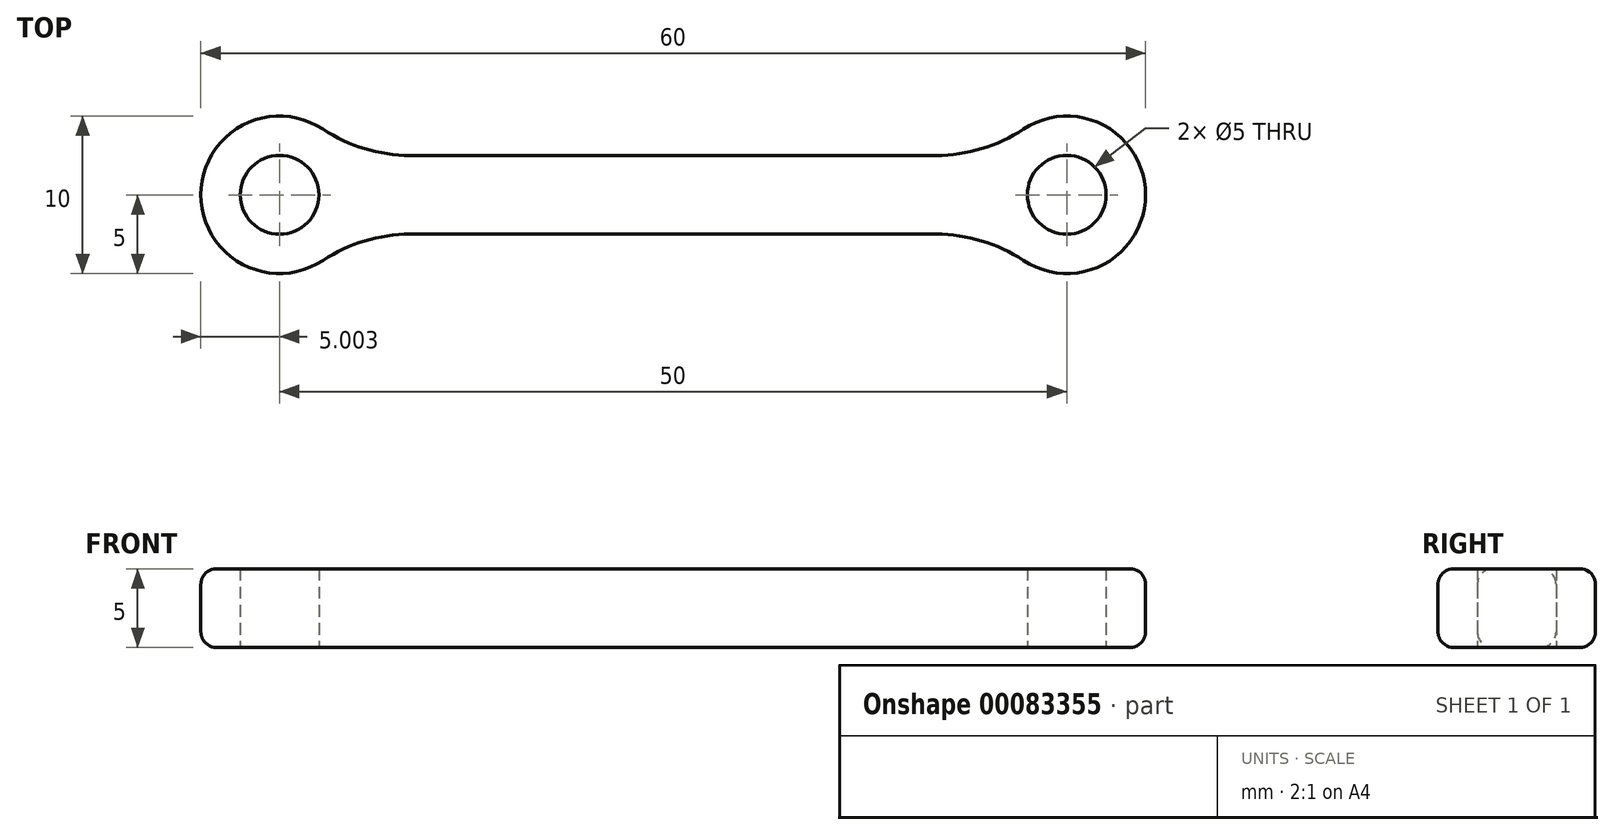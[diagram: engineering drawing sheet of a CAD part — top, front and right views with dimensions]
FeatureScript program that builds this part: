
annotation { "Feature Type Name" : "Feature", "Feature Type Description" : "" }
export const myFeature = defineFeature(function(context is Context, id is Id, definition is map)
    precondition{}
    {
        {
            var Q0;
            Q0=qCreatedBy(makeId("Top.planeOp"),FACE);
            var sketch = newSketch(context, id + "F0", { "sketchPlane" : qUnion([Q0])});
            skLineSegment(sketch, "E0", {"start": v(-7.3, 0) * mm, "end": v(42.7, 0) * mm, "construction": true});
            skCircle(sketch, "E1", {"center": v(-7.3, 0) * mm, "radius": 2.5 * mm});
            skCircle(sketch, "E2", {"center": v(42.7, 0) * mm, "radius": 2.5 * mm});
            skCircle(sketch, "E3", {"center": v(42.7, 0) * mm, "radius": 5 * mm});
            skCircle(sketch, "E4", {"center": v(-7.3, 0) * mm, "radius": 5 * mm});
            skLineSegment(sketch, "E5", {"start": v(-2.98, 2.5) * mm, "end": v(38.36, 2.5) * mm});
            skLineSegment(sketch, "E6", {"start": v(38.36, -2.5) * mm, "end": v(-2.98, -2.5) * mm});
            skSolve(sketch);
        }
        {
            var Q0;
            Q0=makeQuery(id+"F0.imprint","IMPRINT",FACE,{"disambiguationData":[TD([[makeQuery(id+"F0.imprint","IMPRINT",EDGE,{"derivedFrom":sQuery(id+"F0.wireOp",EDGE,"E1")}),-1.0]])]});
            var Q1;
            {var subQ0=sQuery(id+"F0.wireOp",EDGE,"E5");Q1=makeQuery(id+"F0.imprint","IMPRINT",FACE,{"disambiguationData":[TD([[makeQuery(id+"F0.imprint","IMPRINT",EDGE,{"derivedFrom":subQ0}),-1.0]])]});}
            var Q2;
            Q2=makeQuery(id+"F0.imprint","IMPRINT",FACE,{"disambiguationData":[TD([[makeQuery(id+"F0.imprint","IMPRINT",EDGE,{"derivedFrom":sQuery(id+"F0.wireOp",EDGE,"E2")}),-1.0]])]});
            extrude(context, id + "F1", {"entities" : qUnion([Q0, Q1, Q2]), "depth" : 5 * mm});
        }
        {
            var Q0;
            Q0=makeQuery(id+"F1.opExtrude","SWEPT_EDGE",EDGE,{"disambiguationData":[OSD([sQuery(id+"F0.wireOp",EDGE,"E4"),sQuery(id+"F0.wireOp",EDGE,"E5")])]});
            var Q1;
            Q1=makeQuery(id+"F1.opExtrude","SWEPT_EDGE",EDGE,{"disambiguationData":[OSD([sQuery(id+"F0.wireOp",EDGE,"E4"),sQuery(id+"F0.wireOp",EDGE,"E6")])]});
            var Q2;
            Q2=makeQuery(id+"F1.opExtrude","SWEPT_EDGE",EDGE,{"disambiguationData":[OSD([sQuery(id+"F0.wireOp",EDGE,"E3"),sQuery(id+"F0.wireOp",EDGE,"E6")])]});
            var Q3;
            Q3=makeQuery(id+"F1.opExtrude","SWEPT_EDGE",EDGE,{"disambiguationData":[OSD([sQuery(id+"F0.wireOp",EDGE,"E3"),sQuery(id+"F0.wireOp",EDGE,"E5")])]});
            fillet(context, id + "F2", {"entities" : qUnion([Q0, Q1, Q2, Q3]), "radius" : 10 * mm, "tangentPropagation" : true, "allowEdgeOverflow" : false});
        }
        {
            var Q0;
            Q0=makeQuery(id+"F1.opExtrude","CAP_EDGE",EDGE,{"disambiguationData":[OSD([sQuery(id+"F0.wireOp",EDGE,"E5")])],"isStart":false});
            var Q1;
            {var subQ0=sQuery(id+"F0.wireOp",EDGE,"E5");var subQ1=sQuery(id+"F0.wireOp",EDGE,"E4");Q1=makeQuery(id+"F2.opFillet","BLEND_EDGE",EDGE,{"blendedFrom":[makeQuery(id+"F1.opExtrude","SWEPT_EDGE",EDGE,{"disambiguationData":[OSD([subQ1,subQ0])]}),makeQuery(id+"F1.opExtrude","CAP_FACE",FACE,{"disambiguationData":[OSD([sQuery(id+"F0.wireOp",EDGE,"E1"),sQuery(id+"F0.wireOp",EDGE,"E2"),sQuery(id+"F0.wireOp",EDGE,"E3"),subQ1,subQ0,sQuery(id+"F0.wireOp",EDGE,"E6")])],"isStart":false})],"blendedInto":[makeQuery(id+"F1.opExtrude","CAP_FACE",FACE,{"disambiguationData":[OSD([sQuery(id+"F0.wireOp",EDGE,"E1"),sQuery(id+"F0.wireOp",EDGE,"E2"),sQuery(id+"F0.wireOp",EDGE,"E3"),subQ1,subQ0,sQuery(id+"F0.wireOp",EDGE,"E6")])],"isStart":false})]});}
            var Q2;
            Q2=makeQuery(id+"F1.opExtrude","CAP_EDGE",EDGE,{"disambiguationData":[OSD([sQuery(id+"F0.wireOp",EDGE,"E5")])],"isStart":true});
            fillet(context, id + "F3", {"entities" : qUnion([Q0, Q1, Q2]), "radius" : 1 * mm, "tangentPropagation" : true, "allowEdgeOverflow" : false});
        }
    });
